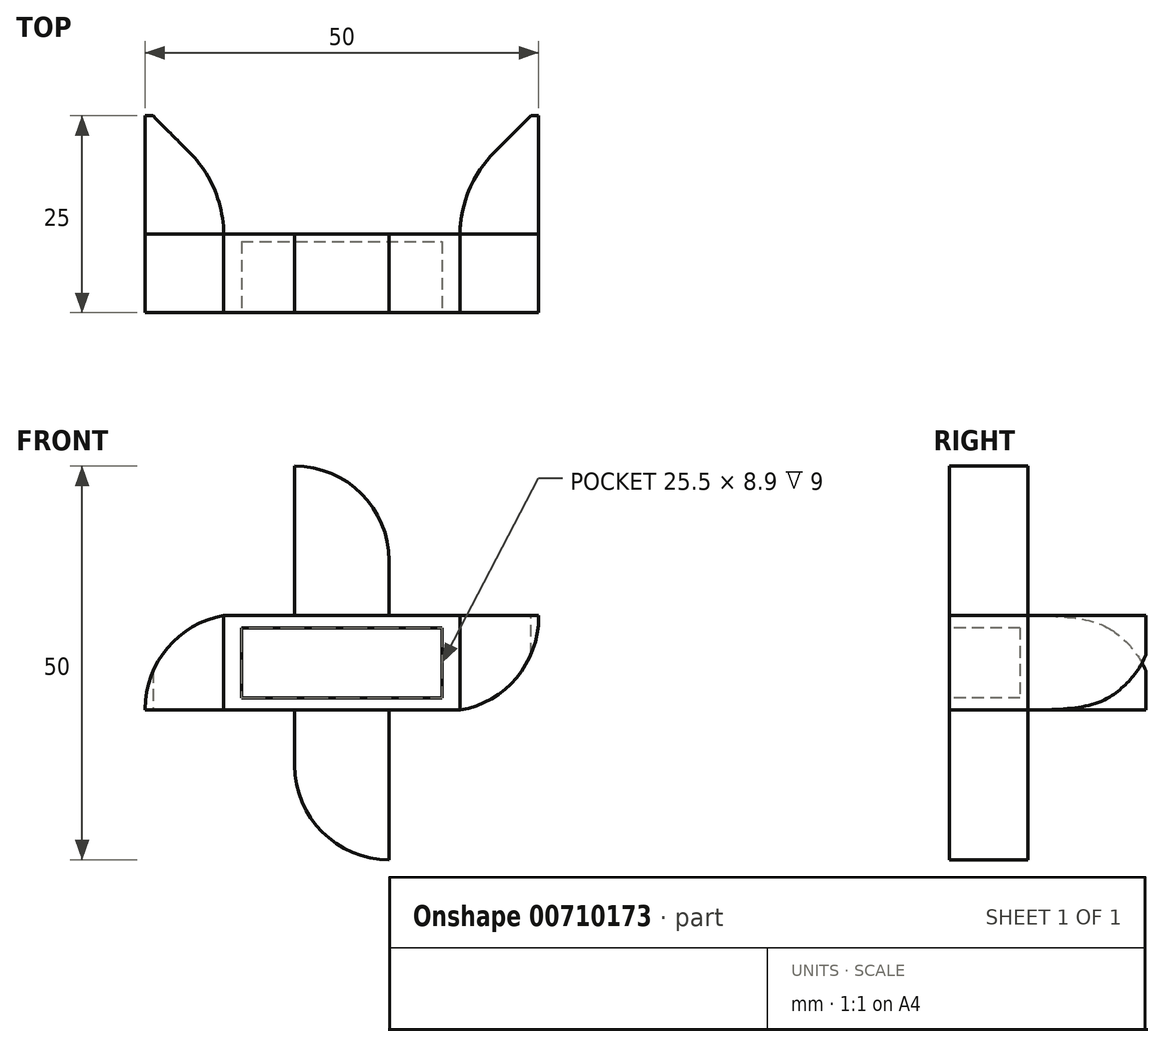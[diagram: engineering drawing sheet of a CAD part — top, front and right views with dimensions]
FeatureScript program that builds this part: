
annotation { "Feature Type Name" : "Feature", "Feature Type Description" : "" }
export const myFeature = defineFeature(function(context is Context, id is Id, definition is map)
    precondition{}
    {
        {
            var Q0;
            Q0=qCreatedBy(makeId("Top.planeOp"),FACE);
            var sketch = newSketch(context, id + "F0", { "sketchPlane" : qUnion([Q0])});
            skLineSegment(sketch, "E0", {"start": v(0, 0) * mm, "end": v(25.5, 0) * mm});
            skLineSegment(sketch, "E1", {"start": v(25.5, 0) * mm, "end": v(25.5, 8.9) * mm});
            skLineSegment(sketch, "E2", {"start": v(25.5, 8.9) * mm, "end": v(0, 8.9) * mm});
            skLineSegment(sketch, "E3", {"start": v(0, 8.9) * mm, "end": v(0, 0) * mm});
            skSolve(sketch);
        }
        {
            var Q0;
            Q0=makeQuery(id+"F0.imprint","IMPRINT",FACE,{"disambiguationData":[TD([[makeQuery(id+"F0.imprint","IMPRINT",EDGE,{"derivedFrom":sQuery(id+"F0.wireOp",EDGE,"E0")}),1.0]])]});
            extrude(context, id + "F1", {"entities" : qUnion([Q0]), "depth" : 8.9 * mm, "offsetDistance" : 25 * mm});
        }
        {
            var Q0;
            Q0=makeQuery(id+"F1.opExtrude","SWEPT_FACE",FACE,{"disambiguationData":[OSD([sQuery(id+"F0.wireOp",EDGE,"E0")])]});
            var sketch = newSketch(context, id + "F2", { "sketchPlane" : qUnion([Q0])});
            skLineSegment(sketch, "E4.bottom", {"start": v(-2.25, 10.45) * mm, "end": v(27.75, 10.45) * mm});
            skLineSegment(sketch, "E4.top", {"start": v(-2.25, -1.55) * mm, "end": v(27.75, -1.55) * mm});
            skLineSegment(sketch, "E4.left", {"start": v(-2.25, 10.45) * mm, "end": v(-2.25, -1.55) * mm});
            skLineSegment(sketch, "E4.right", {"start": v(27.75, 10.45) * mm, "end": v(27.75, -1.55) * mm});
            skPoint(sketch, "E4.middle", {"position": v(12.75, 4.45) * mm});
            skSolve(sketch);
        }
        {
            var Q0;
            {var subQ0=sQuery(id+"F0.wireOp",EDGE,"E0");Q0=makeQuery(id+"F2.imprint","IMPRINT",FACE,{"disambiguationData":[TD([[makeQuery(id+"F2.imprint","IMPRINT",EDGE,{"derivedFrom":makeQuery(id+"F1.opExtrude","CAP_EDGE",EDGE,{"disambiguationData":[OSD([subQ0])],"isStart":true})}),1.0]])]});}
            var Q1;
            Q1=makeQuery(id+"F2.imprint","IMPRINT",FACE,{"disambiguationData":[TD([[makeQuery(id+"F2.imprint","IMPRINT",EDGE,{"derivedFrom":sQuery(id+"F2.wireOp",EDGE,"E4.bottom")}),-1.0]])]});
            extrude(context, id + "F3", {"entities" : qUnion([Q0, Q1]), "oppositeDirection" : true, "depth" : 10 * mm, "offsetDistance" : 25 * mm});
        }
        {
            var Q0;
            Q0=makeQuery(id+"F1.opExtrude","SWEPT_FACE",FACE,{"disambiguationData":[OSD([sQuery(id+"F0.wireOp",EDGE,"E0")])]});
            extrude(context, id + "F4", {"entities" : qUnion([Q0]), "operationType" : NewBodyOperationType.REMOVE, "oppositeDirection" : true, "depth" : 9 * mm, "offsetDistance" : 25 * mm});
        }
        {
            var Q0;
            Q0=makeQuery(id+"F3.opExtrude","SWEPT_FACE",FACE,{"disambiguationData":[OSD([sQuery(id+"F2.wireOp",EDGE,"E4.left")])]});
            extrude(context, id + "F5", {"entities" : qUnion([Q0]), "depth" : 10 * mm, "offsetDistance" : 25 * mm});
        }
        {
            var Q0;
            Q0=makeQuery(id+"F3.opExtrude","SWEPT_FACE",FACE,{"disambiguationData":[OSD([sQuery(id+"F2.wireOp",EDGE,"E4.right")])]});
            extrude(context, id + "F6", {"entities" : qUnion([Q0]), "depth" : 10 * mm, "offsetDistance" : 25 * mm});
        }
        {
            var Q0;
            Q0=makeQuery(id+"F3.opExtrude","SWEPT_FACE",FACE,{"disambiguationData":[OSD([sQuery(id+"F2.wireOp",EDGE,"E4.bottom")])]});
            var sketch = newSketch(context, id + "F7", { "sketchPlane" : qUnion([Q0])});
            skLineSegment(sketch, "E5", {"start": v(12.75, 0) * mm, "end": v(18.75, 0) * mm});
            skLineSegment(sketch, "E6", {"start": v(18.75, 0) * mm, "end": v(18.75, 10) * mm});
            skLineSegment(sketch, "E7", {"start": v(18.75, 10) * mm, "end": v(12.75, 10) * mm});
            skLineSegment(sketch, "E8", {"start": v(12.75, 10) * mm, "end": v(6.75, 10) * mm});
            skLineSegment(sketch, "E9", {"start": v(6.75, 10) * mm, "end": v(6.75, 0) * mm});
            skLineSegment(sketch, "E10", {"start": v(12.75, 0) * mm, "end": v(6.75, 0) * mm});
            skSolve(sketch);
        }
        {
            var Q0;
            Q0=makeQuery(id+"F7.imprint","IMPRINT",FACE,{"disambiguationData":[TD([[makeQuery(id+"F7.imprint","IMPRINT",EDGE,{"derivedFrom":sQuery(id+"F7.wireOp",EDGE,"E5")}),1.0]])]});
            extrude(context, id + "F8", {"entities" : qUnion([Q0]), "depth" : 19 * mm, "offsetDistance" : 25 * mm});
        }
        {
            var Q0;
            Q0=makeQuery(id+"F3.opExtrude","SWEPT_FACE",FACE,{"disambiguationData":[OSD([sQuery(id+"F2.wireOp",EDGE,"E4.top")])]});
            var sketch = newSketch(context, id + "F9", { "sketchPlane" : qUnion([Q0])});
            skLineSegment(sketch, "E11", {"start": v(12.75, -10) * mm, "end": v(18.75, -10) * mm});
            skLineSegment(sketch, "E12", {"start": v(18.75, -10) * mm, "end": v(18.75, 0) * mm});
            skLineSegment(sketch, "E13", {"start": v(12.75, 0) * mm, "end": v(18.75, 0) * mm});
            skLineSegment(sketch, "E14", {"start": v(12.75, 0) * mm, "end": v(6.75, 0) * mm});
            skLineSegment(sketch, "E15", {"start": v(6.75, 0) * mm, "end": v(6.75, -10) * mm});
            skLineSegment(sketch, "E16", {"start": v(6.75, -10) * mm, "end": v(12.75, -10) * mm});
            skSolve(sketch);
        }
        {
            var Q0;
            Q0=makeQuery(id+"F9.imprint","IMPRINT",FACE,{"disambiguationData":[TD([[makeQuery(id+"F9.imprint","IMPRINT",EDGE,{"derivedFrom":sQuery(id+"F9.wireOp",EDGE,"E11")}),1.0]])]});
            extrude(context, id + "F10", {"entities" : qUnion([Q0]), "depth" : 19 * mm, "offsetDistance" : 25 * mm});
        }
        {
            var Q0;
            Q0=makeQuery(id+"F10.opExtrude","CAP_EDGE",EDGE,{"disambiguationData":[OSD([sQuery(id+"F9.wireOp",EDGE,"E15")])],"isStart":false});
            var Q1;
            Q1=makeQuery(id+"F5.opExtrude","CAP_EDGE",EDGE,{"disambiguationData":[OSD([sQuery(id+"F2.wireOp",EDGE,"E4.bottom"),sQuery(id+"F2.wireOp",EDGE,"E4.left")])],"isStart":false});
            var Q2;
            Q2=makeQuery(id+"F8.opExtrude","CAP_EDGE",EDGE,{"disambiguationData":[OSD([sQuery(id+"F7.wireOp",EDGE,"E6")])],"isStart":false});
            var Q3;
            Q3=makeQuery(id+"F6.opExtrude","CAP_EDGE",EDGE,{"disambiguationData":[OSD([sQuery(id+"F2.wireOp",EDGE,"E4.top"),sQuery(id+"F2.wireOp",EDGE,"E4.right")])],"isStart":false});
            fillet(context, id + "F11", {"entities" : qUnion([Q0, Q1, Q2, Q3]), "radius" : 12 * mm, "tangentPropagation" : true, "allowEdgeOverflow" : false});
        }
        {
            var Q0;
            Q0=makeQuery(id+"F10.boolean.opBoolean","MERGE",FACE,{"derivedFrom":[makeQuery(id+"F8.boolean.opBoolean","MERGE",FACE,{"derivedFrom":[makeQuery(id+"F3.opExtrude","CAP_FACE",FACE,{"disambiguationData":[OSD([sQuery(id+"F2.wireOp",EDGE,"E4.bottom"),sQuery(id+"F2.wireOp",EDGE,"E4.top"),sQuery(id+"F2.wireOp",EDGE,"E4.left"),sQuery(id+"F2.wireOp",EDGE,"E4.right")])],"isStart":false}),makeQuery(id+"F8.opExtrude","SWEPT_FACE",FACE,{"disambiguationData":[OSD([sQuery(id+"F7.wireOp",EDGE,"E7"),sQuery(id+"F7.wireOp",EDGE,"E8")])]})]}),makeQuery(id+"F10.opExtrude","SWEPT_FACE",FACE,{"disambiguationData":[OSD([sQuery(id+"F9.wireOp",EDGE,"E11"),sQuery(id+"F9.wireOp",EDGE,"E16")])]})]});
            var sketch = newSketch(context, id + "F12", { "sketchPlane" : qUnion([Q0])});
            skLineSegment(sketch, "E17", {"start": v(-18.75, 10.45) * mm, "end": v(-18.75, -1.55) * mm});
            skLineSegment(sketch, "E18", {"start": v(-18.75, -1.55) * mm, "end": v(-6.75, -1.55) * mm});
            skLineSegment(sketch, "E19", {"start": v(-6.75, -1.55) * mm, "end": v(-6.75, 10.45) * mm});
            skLineSegment(sketch, "E20", {"start": v(-6.75, 10.45) * mm, "end": v(-18.75, 10.45) * mm});
            skLineSegment(sketch, "E21", {"start": v(-18.75, 17.45) * mm, "end": v(-6.75, 17.45) * mm});
            skLineSegment(sketch, "E22", {"start": v(-6.75, -8.55) * mm, "end": v(-18.75, -8.55) * mm});
            skSolve(sketch);
        }
        {
            var Q0;
            {var subQ0=sQuery(id+"F12.wireOp",EDGE,"E22");Q0=makeQuery(id+"F12.imprint","IMPRINT",FACE,{"disambiguationData":[TD([[makeQuery(id+"F12.imprint","IMPRINT",EDGE,{"derivedFrom":subQ0}),1.0]])]});}
            var Q1;
            {var subQ0=sQuery(id+"F2.wireOp",EDGE,"E4.right");Q1=makeQuery(id+"F6.opExtrude","SWEPT_FACE",FACE,{"disambiguationData":[OSD([subQ0]),TDD([makeQuery(id+"F3.opExtrude","CAP_EDGE",EDGE,{"disambiguationData":[OSD([subQ0])],"isStart":false})])]});}
            var Q2;
            {var subQ0=sQuery(id+"F12.wireOp",EDGE,"E21");Q2=makeQuery(id+"F12.imprint","IMPRINT",FACE,{"disambiguationData":[TD([[makeQuery(id+"F12.imprint","IMPRINT",EDGE,{"derivedFrom":subQ0}),1.0]])]});}
            var Q3;
            {var subQ0=sQuery(id+"F2.wireOp",EDGE,"E4.left");Q3=makeQuery(id+"F5.opExtrude","SWEPT_FACE",FACE,{"disambiguationData":[OSD([subQ0]),TDD([makeQuery(id+"F3.opExtrude","CAP_EDGE",EDGE,{"disambiguationData":[OSD([subQ0])],"isStart":false})])]});}
            extrude(context, id + "F13", {"entities" : qUnion([Q0, Q1, Q2, Q3]), "depth" : 15 * mm, "offsetDistance" : 25 * mm});
        }
        {
            var Q0;
            {var subQ0=sQuery(id+"F2.wireOp",EDGE,"E4.left");Q0=makeQuery(id+"F13.opExtrude","CAP_EDGE",EDGE,{"disambiguationData":[OSD([subQ0]),TDD([makeQuery(id+"F5.opExtrude","CAP_EDGE",EDGE,{"disambiguationData":[OSD([subQ0]),TDD([makeQuery(id+"F3.opExtrude","CAP_EDGE",EDGE,{"disambiguationData":[OSD([subQ0])],"isStart":false})])],"isStart":true})])],"isStart":false});}
            var Q1;
            Q1=makeQuery(id+"F13.opExtrude","CAP_EDGE",EDGE,{"disambiguationData":[OSD([sQuery(id+"F12.wireOp",EDGE,"E21")])],"isStart":false});
            var Q2;
            {var subQ0=sQuery(id+"F2.wireOp",EDGE,"E4.right");Q2=makeQuery(id+"F13.opExtrude","CAP_EDGE",EDGE,{"disambiguationData":[OSD([subQ0]),TDD([makeQuery(id+"F6.opExtrude","CAP_EDGE",EDGE,{"disambiguationData":[OSD([subQ0]),TDD([makeQuery(id+"F3.opExtrude","CAP_EDGE",EDGE,{"disambiguationData":[OSD([subQ0])],"isStart":false})])],"isStart":true})])],"isStart":false});}
            var Q3;
            Q3=makeQuery(id+"F13.opExtrude","CAP_EDGE",EDGE,{"disambiguationData":[OSD([sQuery(id+"F12.wireOp",EDGE,"E22")])],"isStart":false});
            chamfer(context, id + "F14", {"entities" : qUnion([Q0, Q1, Q2, Q3]), "width" : 9 * mm, "tangentPropagation" : true});
        }
        {
            var Q0;
            {var subQ0=sQuery(id+"F2.wireOp",EDGE,"E4.left");var subQ1=makeQuery(id+"F5.opExtrude","CAP_EDGE",EDGE,{"disambiguationData":[OSD([subQ0]),TDD([makeQuery(id+"F3.opExtrude","CAP_EDGE",EDGE,{"disambiguationData":[OSD([subQ0])],"isStart":false})])],"isStart":true});Q0=makeQuery(id+"F14.opChamfer","BLEND_EDGE",EDGE,{"blendedFrom":[makeQuery(id+"F13.opExtrude","CAP_EDGE",EDGE,{"disambiguationData":[OSD([subQ0]),TDD([subQ1])],"isStart":false}),makeQuery(id+"F13.opExtrude","SWEPT_FACE",FACE,{"disambiguationData":[OSD([subQ0]),TDD([subQ1])]})],"blendedInto":[makeQuery(id+"F13.opExtrude","SWEPT_FACE",FACE,{"disambiguationData":[OSD([subQ0]),TDD([subQ1])]})]});}
            var Q1;
            {var subQ0=sQuery(id+"F12.wireOp",EDGE,"E21");Q1=makeQuery(id+"F14.opChamfer","BLEND_EDGE",EDGE,{"blendedFrom":[makeQuery(id+"F13.opExtrude","CAP_EDGE",EDGE,{"disambiguationData":[OSD([subQ0])],"isStart":false}),makeQuery(id+"F13.opExtrude","SWEPT_FACE",FACE,{"disambiguationData":[OSD([subQ0])]})],"blendedInto":[makeQuery(id+"F13.opExtrude","SWEPT_FACE",FACE,{"disambiguationData":[OSD([subQ0])]})]});}
            var Q2;
            {var subQ0=sQuery(id+"F12.wireOp",EDGE,"E22");Q2=makeQuery(id+"F14.opChamfer","BLEND_EDGE",EDGE,{"blendedFrom":[makeQuery(id+"F13.opExtrude","CAP_EDGE",EDGE,{"disambiguationData":[OSD([subQ0])],"isStart":false}),makeQuery(id+"F13.opExtrude","SWEPT_FACE",FACE,{"disambiguationData":[OSD([subQ0])]})],"blendedInto":[makeQuery(id+"F13.opExtrude","SWEPT_FACE",FACE,{"disambiguationData":[OSD([subQ0])]})]});}
            var Q3;
            {var subQ0=sQuery(id+"F2.wireOp",EDGE,"E4.right");var subQ1=makeQuery(id+"F6.opExtrude","CAP_EDGE",EDGE,{"disambiguationData":[OSD([subQ0]),TDD([makeQuery(id+"F3.opExtrude","CAP_EDGE",EDGE,{"disambiguationData":[OSD([subQ0])],"isStart":false})])],"isStart":true});Q3=makeQuery(id+"F14.opChamfer","BLEND_EDGE",EDGE,{"blendedFrom":[makeQuery(id+"F13.opExtrude","CAP_EDGE",EDGE,{"disambiguationData":[OSD([subQ0]),TDD([subQ1])],"isStart":false}),makeQuery(id+"F13.opExtrude","SWEPT_FACE",FACE,{"disambiguationData":[OSD([subQ0]),TDD([subQ1])]})],"blendedInto":[makeQuery(id+"F13.opExtrude","SWEPT_FACE",FACE,{"disambiguationData":[OSD([subQ0]),TDD([subQ1])]})]});}
            fillet(context, id + "F15", {"entities" : qUnion([Q0, Q1, Q2, Q3]), "radius" : 15 * mm, "tangentPropagation" : true, "allowEdgeOverflow" : false});
        }
    });
